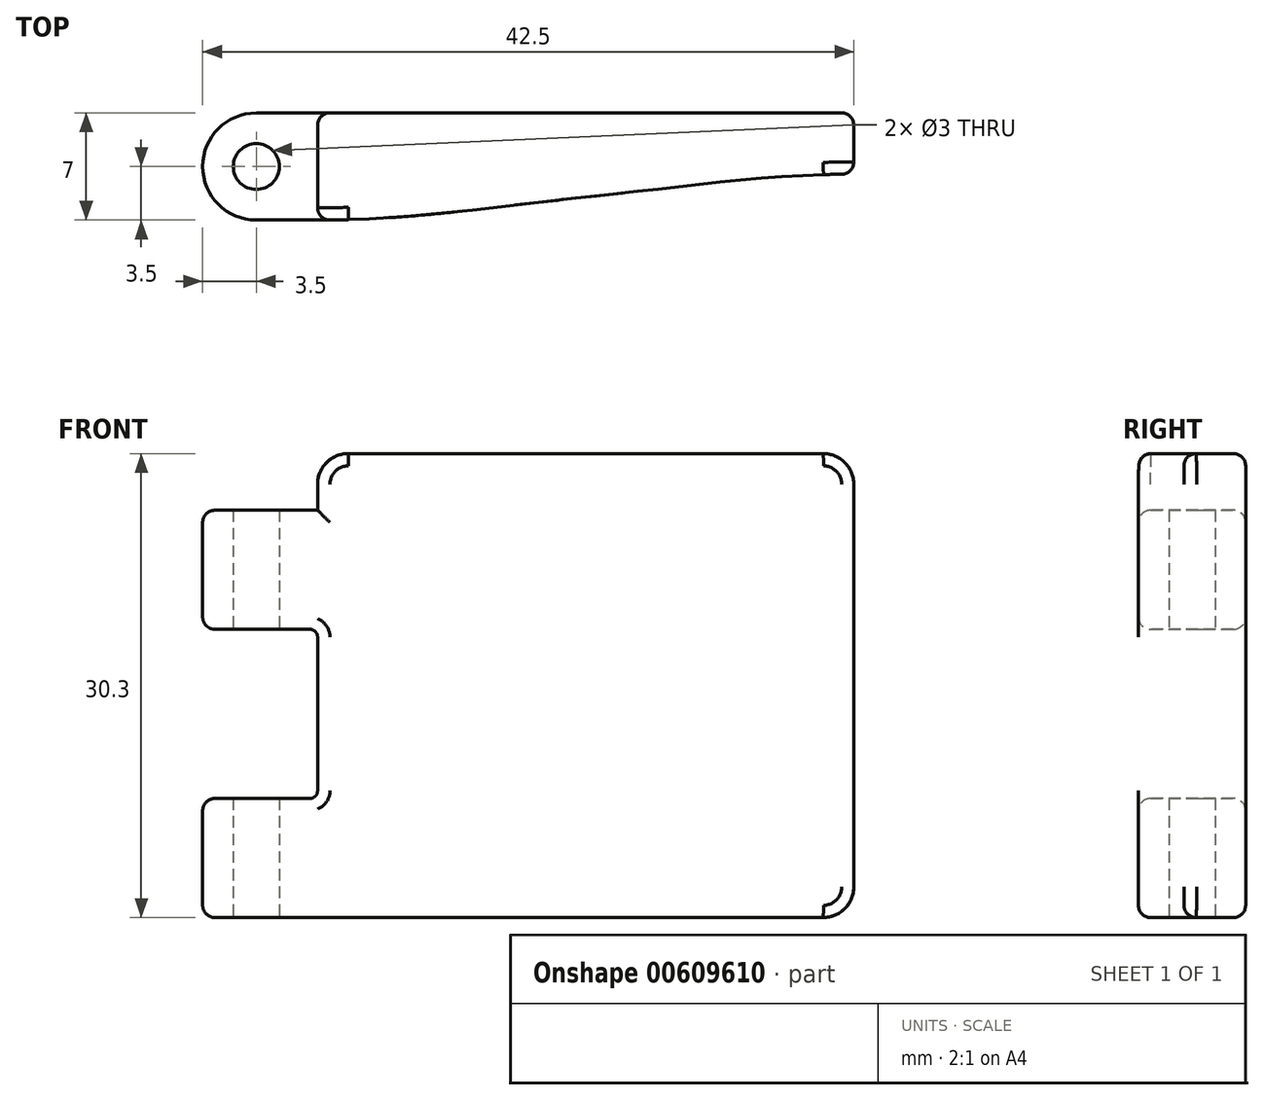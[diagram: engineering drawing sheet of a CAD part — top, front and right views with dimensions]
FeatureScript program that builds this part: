
annotation { "Feature Type Name" : "Feature", "Feature Type Description" : "" }
export const myFeature = defineFeature(function(context is Context, id is Id, definition is map)
    precondition{}
    {
        {
            var Q0;
            Q0=qCreatedBy(makeId("Top.planeOp"),FACE);
            var sketch = newSketch(context, id + "F0", { "sketchPlane" : qUnion([Q0])});
            skCircle(sketch, "E0", {"center": v(-4, -3.5) * mm, "radius": 3.5 * mm, "construction": true});
            skCircle(sketch, "E1", {"center": v(-4, -3.5) * mm, "radius": 1.5 * mm});
            skLineSegment(sketch, "E2", {"start": v(-4, -7) * mm, "end": v(0, -7) * mm});
            skLineSegment(sketch, "E3", {"start": v(-4, 0) * mm, "end": v(0, 0) * mm});
            skArc(sketch, "E4", {"start": v(-4, 0) * mm, "mid": v(-7.5, -3.5) * mm, "end": v(-4, -7) * mm});
            skLineSegment(sketch, "E5", {"start": v(0, -7) * mm, "end": v(0, 0) * mm});
            skSolve(sketch);
        }
        {
            var Q0;
            Q0=qSketchRegion(id+"F0",true);
            extrude(context, id + "F1", {"entities" : qUnion([Q0]), "endBound" : BoundingType.SYMMETRIC, "depth" : 26.6 * mm, "offsetDistance" : 25 * mm});
        }
        {
            var Q0;
            Q0=qCreatedBy(makeId("Top.planeOp"),FACE);
            var sketch = newSketch(context, id + "F2", { "sketchPlane" : qUnion([Q0])});
            skLineSegment(sketch, "E6", {"start": v(0, 0) * mm, "end": v(35, 0) * mm});
            skLineSegment(sketch, "E7", {"start": v(35, 0) * mm, "end": v(35, -4) * mm});
            skFitSpline(sketch, "E8", {"points": [v(35, -4) * mm, v(22, -5) * mm, v(13, -6) * mm, v(0, -7) * mm], "startDerivative": vector(-42.5, 0) * mm, "endDerivative": vector(-42.5, 0) * mm});
            skLineSegment(sketch, "E9", {"start": v(0, 0) * mm, "end": v(0, -7) * mm});
            skSolve(sketch);
        }
        {
            var Q0;
            Q0=makeQuery(id+"F2.imprint","IMPRINT",FACE,{"disambiguationData":[TD([[makeQuery(id+"F2.imprint","IMPRINT",EDGE,{"derivedFrom":sQuery(id+"F2.wireOp",EDGE,"E6")}),-1.0]])]});
            var Q1;
            Q1=makeQuery(id+"F1.opExtrude","CAP_FACE",FACE,{"disambiguationData":[OSD([sQuery(id+"F0.wireOp",EDGE,"E1"),sQuery(id+"F0.wireOp",EDGE,"E2"),sQuery(id+"F0.wireOp",EDGE,"E3"),sQuery(id+"F0.wireOp",EDGE,"E4"),sQuery(id+"F0.wireOp",EDGE,"E5")])],"isStart":true});
            extrude(context, id + "F3", {"entities" : qUnion([Q0]), "operationType" : NewBodyOperationType.ADD, "depth" : 17 * mm, "offsetDistance" : 25 * mm, "hasSecondDirection" : true, "secondDirectionBound" : SecondDirectionBoundingType.UP_TO_SURFACE, "secondDirectionOppositeDirection" : true, "secondDirectionDepth" : 25 * mm, "secondDirectionBoundEntityFace" : qUnion([Q1])});
        }
        {
            var Q0;
            Q0=qSketchRegion(id+"F0",true);
            extrude(context, id + "F4", {"entities" : qUnion([Q0]), "operationType" : NewBodyOperationType.REMOVE, "endBound" : BoundingType.SYMMETRIC, "depth" : 11.05 * mm, "offsetDistance" : 25 * mm});
        }
        {
            var Q0;
            Q0=makeQuery(id+"F1.opExtrude","CAP_EDGE",EDGE,{"disambiguationData":[OSD([sQuery(id+"F0.wireOp",EDGE,"E5")])],"isStart":false});
            var Q1;
            Q1=makeQuery(id+"F4.boolean.opBoolean","COPY",EDGE,{"derivedFrom":makeQuery(id+"F4.opExtrude","CAP_EDGE",EDGE,{"disambiguationData":[OSD([sQuery(id+"F0.wireOp",EDGE,"E5")])],"isStart":false})});
            var Q2;
            Q2=makeQuery(id+"F4.boolean.opBoolean","COPY",EDGE,{"derivedFrom":makeQuery(id+"F4.opExtrude","CAP_EDGE",EDGE,{"disambiguationData":[OSD([sQuery(id+"F0.wireOp",EDGE,"E5")])],"isStart":true})});
            fillet(context, id + "F5", {"entities" : qUnion([Q0, Q1, Q2]), "radius" : 0.5 * mm, "tangentPropagation" : true, "allowEdgeOverflow" : false});
        }
        {
            var Q0;
            Q0=makeQuery(id+"F3.opExtrude","CAP_EDGE",EDGE,{"disambiguationData":[OSD([sQuery(id+"F2.wireOp",EDGE,"E9")])],"isStart":false});
            var Q1;
            Q1=makeQuery(id+"F3.opExtrude","CAP_EDGE",EDGE,{"disambiguationData":[OSD([sQuery(id+"F2.wireOp",EDGE,"E7")])],"isStart":false});
            var Q2;
            Q2=makeQuery(id+"F3.opExtrude","CAP_EDGE",EDGE,{"disambiguationData":[OSD([sQuery(id+"F2.wireOp",EDGE,"E7")])],"isStart":true});
            fillet(context, id + "F6", {"entities" : qUnion([Q0, Q1, Q2]), "radius" : 2 * mm, "tangentPropagation" : true, "allowEdgeOverflow" : false});
        }
        {
            var Q0;
            Q0=makeQuery(id+"F3.opExtrude","SWEPT_FACE",FACE,{"disambiguationData":[OSD([sQuery(id+"F2.wireOp",EDGE,"E8")])]});
            var Q1;
            Q1=makeQuery(id+"F3.boolean.opBoolean","MERGE",FACE,{"derivedFrom":[makeQuery(id+"F1.opExtrude","SWEPT_FACE",FACE,{"disambiguationData":[OSD([sQuery(id+"F0.wireOp",EDGE,"E3")])]}),makeQuery(id+"F3.opExtrude","SWEPT_FACE",FACE,{"disambiguationData":[OSD([sQuery(id+"F2.wireOp",EDGE,"E6")])]})]});
            fillet(context, id + "F7", {"entities" : qUnion([Q0, Q1]), "radius" : 0.8 * mm, "tangentPropagation" : true, "allowEdgeOverflow" : false});
        }
    });
